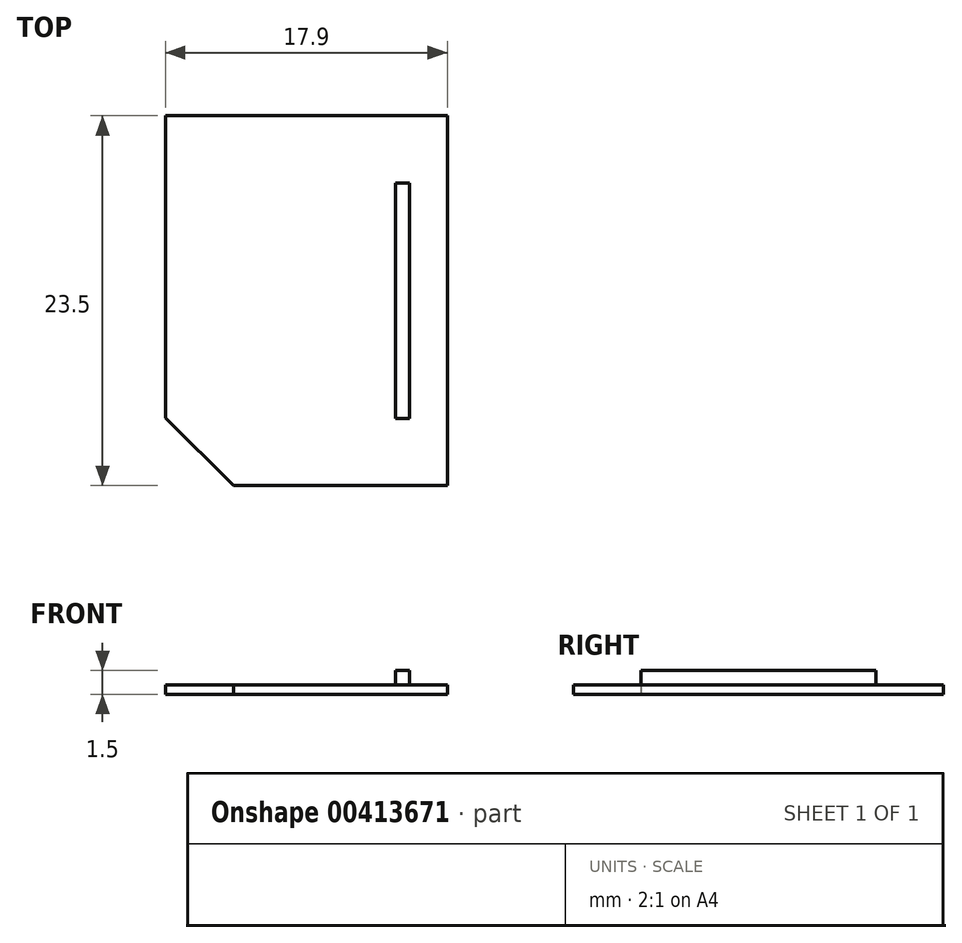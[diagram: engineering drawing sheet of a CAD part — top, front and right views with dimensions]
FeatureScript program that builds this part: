
annotation { "Feature Type Name" : "Feature", "Feature Type Description" : "" }
export const myFeature = defineFeature(function(context is Context, id is Id, definition is map)
    precondition{}
    {
        {
            var Q0;
            Q0=qCreatedBy(makeId("Top.planeOp"),FACE);
            var sketch = newSketch(context, id + "F0", { "sketchPlane" : qUnion([Q0])});
            skLineSegment(sketch, "E0", {"start": v(-22.84, 19.92) * mm, "end": v(-4.94, 19.92) * mm});
            skLineSegment(sketch, "E1", {"start": v(-4.94, 19.92) * mm, "end": v(-4.94, -3.58) * mm});
            skLineSegment(sketch, "E2", {"start": v(-4.94, -3.58) * mm, "end": v(-18.54, -3.58) * mm});
            skLineSegment(sketch, "E3", {"start": v(-18.54, -3.58) * mm, "end": v(-22.84, 0.72) * mm});
            skLineSegment(sketch, "E4", {"start": v(-22.84, 0.72) * mm, "end": v(-22.84, 19.92) * mm});
            skSolve(sketch);
        }
        {
            var Q0;
            Q0 = qSketchRegion(id + "F0", true);
            extrude(context, id + "F1", {"entities" : qUnion([Q0]), "depth" : .6 * mm});
        }
        {
            var Q0;
            Q0=makeQuery(id+"F1.opExtrude","CAP_FACE",FACE,{"disambiguationData":[OSD([sQuery(id+"F0.wireOp",EDGE,"E0"),sQuery(id+"F0.wireOp",EDGE,"E1"),sQuery(id+"F0.wireOp",EDGE,"E2"),sQuery(id+"F0.wireOp",EDGE,"E3"),sQuery(id+"F0.wireOp",EDGE,"E4")])],"isStart":false});
            var sketch = newSketch(context, id + "F2", { "sketchPlane" : qUnion([Q0])});
            skLineSegment(sketch, "E5", {"start": v(-7.34, 15.64) * mm, "end": v(-7.34, 0.7) * mm});
            skLineSegment(sketch, "E6.0", {"start": v(-8.24, 15.64) * mm, "end": v(-8.24, 0.7) * mm});
            skLineSegment(sketch, "E7.0", {"start": v(-8.24, 15.64) * mm, "end": v(-7.34, 15.64) * mm});
            skLineSegment(sketch, "E8.0", {"start": v(-8.24, 0.7) * mm, "end": v(-7.34, 0.7) * mm});
            skSolve(sketch);
        }
        {
            var Q0;
            Q0 = qSketchRegion(id + "F2", true);
            extrude(context, id + "F3", {"entities" : qUnion([Q0]), "operationType" : NewBodyOperationType.ADD, "depth" : .9 * mm});
        }
    });
